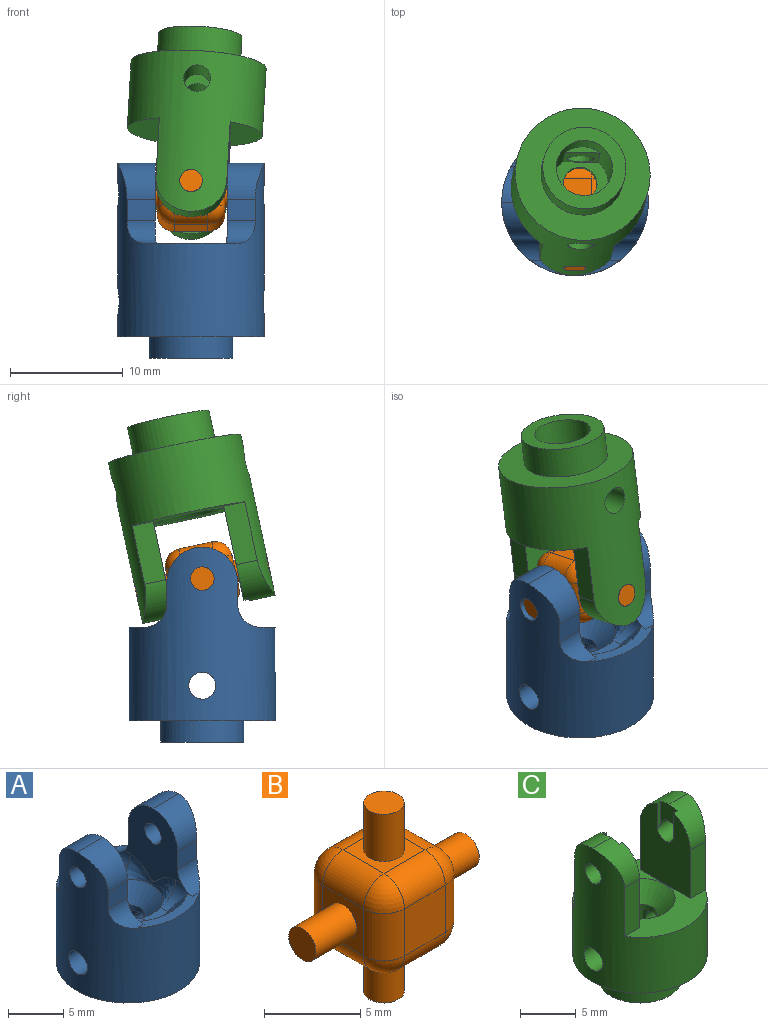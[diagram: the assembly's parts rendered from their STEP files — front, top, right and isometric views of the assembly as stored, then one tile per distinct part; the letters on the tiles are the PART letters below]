
ASSEMBLY  parts=3 mates=2
PART A: 42 faces, bbox 13x13x17.3 mm
  f0: plane 2.4x1.15mm, normal (0,0,1), area 2.2mm2, adj f23,f31,f36,f39
  f1: plane 2.4x1.15mm, normal (0,0,1), area 2.2mm2, adj f26,f31,f38,f41
  f2: plane 2.49x1.93mm, normal (0,1,0), area 4.8mm2, adj f4,f14,f29,f32
  f3: plane 2.49x1.93mm, normal (0,-1,0), area 4.8mm2, adj f4,f14,f30,f33
  f4: plane 8.06x7.39mm, normal (1,0,0), area 37mm2, adj f2,f3,f20,f29,f30,f32,f33,f39
  f5: plane 2.49x1.93mm, normal (0,1,0), area 4.8mm2, adj f6,f14,f27,f34
  f6: plane 8.06x7.39mm, normal (-1,0,0), area 37mm2, adj f5,f7,f19,f27,f28,f34,f35,f36
  f7: plane 2.49x1.93mm, normal (0,-1,0), area 4.8mm2, adj f6,f14,f28,f35
  f8: cylinder r=2.5mm len=6.6mm, axis (0,0,-1), area 71.9mm2, adj f10,f11,f13,f15,f16,f18
  f9: cylinder r=3.7mm len=7.4mm, axis (0,0,-1), area 44.2mm2, adj f10,f12
  f10: plane 7.4x7.4mm, normal (0,0,-1), area 23.4mm2, adj f8,f9
  f11: plane 3.13x0.55mm, normal (0,0,-1), area 1.2mm2, adj f8,f15
  f12: plane 13x13mm, normal (0,0,-1), area 89.7mm2, adj f9,f14
  f13: plane 4.7x3.13mm, normal (-1,0,0), area 10.2mm2, adj f8,f16,f18,f22
  f14: cylinder r=6.5mm len=15.4mm, axis (0,0,-1), area 416.5mm2, adj f2,f3,f5,f7,f12,f19,f20,f21
  f15: plane 4.7x3.13mm, normal (1,0,0), area 10.2mm2, adj f8,f11,f18,f21
  f16: plane 3.13x0.55mm, normal (0,0,-1), area 1.2mm2, adj f8,f13
  f17: cylinder r=1.5mm len=3mm, axis (0,0,-1), area 5.2mm2, adj f18,f31
  f18: plane 5x3.9mm, normal (0,0,-1), area 10.2mm2, adj f8,f13,f15,f17
  f19: cylinder r=1.05mm len=3.3mm, axis (1,0,0), area 21.8mm2, adj f6,f14
  f20: cylinder r=1.05mm len=3.3mm, axis (1,0,0), area 21.8mm2, adj f4,f14
  f21: cylinder r=1.2mm len=4.55mm, axis (1,0,0), area 34.3mm2, adj f14,f15
  f22: cylinder r=1.2mm len=4.55mm, axis (1,0,0), area 34.3mm2, adj f13,f14
  f23: sphere r=7mm, area 10.7mm2, adj f0,f24,f36,f39
  f24: plane 7.93x1.96mm, normal (0,0,1), area 7mm2, adj f14,f23,f33,f35,f36,f39
  f25: plane 7.93x1.96mm, normal (0,0,1), area 7mm2, adj f14,f26,f32,f34,f38,f41
  f26: sphere r=7mm, area 10.7mm2, adj f1,f25,f38,f41
  f27: cylinder r=3.2mm len=3.3mm, axis (1,0,0), area 14.4mm2, adj f5,f6,f14,f28
  f28: cylinder r=3.2mm len=3.3mm, axis (-1,0,0), area 14.4mm2, adj f6,f7,f14,f27
  f29: cylinder r=3.2mm len=3.3mm, axis (1,0,0), area 14.4mm2, adj f2,f4,f14,f30
  f30: cylinder r=3.2mm len=3.3mm, axis (-1,0,0), area 14.4mm2, adj f3,f4,f14,f29
  f31: cone r=1.5mm half-angle=45deg, axis (0,0,1), area 34.1mm2, adj f0,f1,f17,f37,f40
  f32: cylinder r=2mm len=2.59mm, axis (-1,0,0), area 6.2mm2, adj f2,f4,f14,f25,f41
  f33: cylinder r=2mm len=2.59mm, axis (1,0,0), area 6.2mm2, adj f3,f4,f14,f24,f39
  f34: cylinder r=2mm len=2.59mm, axis (-1,0,0), area 6.2mm2, adj f5,f6,f14,f25,f38
  f35: cylinder r=2mm len=2.59mm, axis (1,0,0), area 6.2mm2, adj f6,f7,f14,f24,f36
  f36: cylinder r=2mm len=2.24mm, axis (0,-1,0), area 3.7mm2, adj f0,f6,f23,f24,f35,f37
  f37: bspline ~5.83x2mm, area 9.6mm2, adj f6,f31,f36,f38
  f38: cylinder r=2mm len=2.24mm, axis (0,-1,0), area 3.7mm2, adj f1,f6,f25,f26,f34,f37
  f39: cylinder r=2mm len=2.24mm, axis (0,1,0), area 3.7mm2, adj f0,f4,f23,f24,f33,f40
  f40: bspline ~5.83x2mm, area 9.6mm2, adj f4,f31,f39,f41
  f41: cylinder r=2mm len=2.24mm, axis (0,1,0), area 3.7mm2, adj f1,f4,f25,f26,f32,f40
PART B: 34 faces, bbox 12x6x12 mm
  f0: plane 3x3mm, normal (-1,0,0), area 5.9mm2, adj f12,f22,f27,f30,f33
  f1: plane 3x3mm, normal (0,-1,0), area 9mm2, adj f19,f28,f29,f33
  f2: plane 3x3mm, normal (1,0,0), area 5.9mm2, adj f11,f14,f18,f19,f20
  f3: plane 3x3mm, normal (0,1,0), area 9mm2, adj f14,f17,f21,f22
  f4: plane 3x3mm, normal (0,0,1), area 5.5mm2, adj f8,f17,f18,f27,f28
  f5: plane 3x3mm, normal (0,0,-1), area 5.5mm2, adj f7,f20,f21,f29,f30
  f6: plane 2.1x2.1mm, normal (0,0,-1), area 3.5mm2, adj f7
  f7: cylinder r=1.05mm len=3mm, axis (0,0,-1), area 19.8mm2, adj f5,f6
  f8: cylinder r=1.05mm len=3mm, axis (0,0,-1), area 19.8mm2, adj f4,f9
  f9: plane 2.1x2.1mm, normal (0,0,1), area 3.5mm2, adj f8
  f10: plane 2x2mm, normal (1,0,0), area 3.1mm2, adj f11
  f11: cylinder r=1mm len=3mm, axis (-1,0,0), area 18.8mm2, adj f2,f10
  f12: cylinder r=1mm len=3mm, axis (-1,0,0), area 18.8mm2, adj f0,f13
  f13: plane 2x2mm, normal (-1,0,0), area 3.1mm2, adj f12
  f14: cylinder r=1.5mm len=3mm, axis (0,0,1), area 7.1mm2, adj f2,f3,f15,f16
  f15: sphere r=1.5mm, area 3.5mm2, adj f14,f17,f18
  f16: sphere r=1.5mm, area 3.5mm2, adj f14,f20,f21
  f17: cylinder r=1.5mm len=3mm, axis (1,0,0), area 7.1mm2, adj f3,f4,f15,f23
  f18: cylinder r=1.5mm len=3mm, axis (0,-1,0), area 7.1mm2, adj f2,f4,f15,f24
  f19: cylinder r=1.5mm len=3mm, axis (0,0,-1), area 7.1mm2, adj f1,f2,f24,f25
  f20: cylinder r=1.5mm len=3mm, axis (0,1,0), area 7.1mm2, adj f2,f5,f16,f25
  f21: cylinder r=1.5mm len=3mm, axis (-1,0,0), area 7.1mm2, adj f3,f5,f16,f26
  f22: cylinder r=1.5mm len=3mm, axis (0,0,-1), area 7.1mm2, adj f0,f3,f23,f26
  f23: sphere r=1.5mm, area 3.5mm2, adj f17,f22,f27
  f24: sphere r=1.5mm, area 3.5mm2, adj f18,f19,f28
  f25: sphere r=1.5mm, area 3.5mm2, adj f19,f20,f29
  f26: sphere r=1.5mm, area 3.5mm2, adj f21,f22,f30
  f27: cylinder r=1.5mm len=3mm, axis (0,1,0), area 7.1mm2, adj f0,f4,f23,f31
  f28: cylinder r=1.5mm len=3mm, axis (-1,0,0), area 7.1mm2, adj f1,f4,f24,f31
  f29: cylinder r=1.5mm len=3mm, axis (1,0,0), area 7.1mm2, adj f1,f5,f25,f32
  f30: cylinder r=1.5mm len=3mm, axis (0,-1,0), area 7.1mm2, adj f0,f5,f26,f32
  f31: sphere r=1.5mm, area 3.5mm2, adj f27,f28,f33
  f32: sphere r=1.5mm, area 3.5mm2, adj f29,f30,f33
  f33: cylinder r=1.5mm len=3mm, axis (0,0,1), area 7.1mm2, adj f0,f1,f31,f32
PART C: 37 faces, bbox 12x12x17.3 mm
  f0: plane 8.31x6.3mm, normal (1,0,0), area 41.8mm2, adj f3,f4,f16,f17,f22,f23,f25,f26
  f1: plane 8.31x6.3mm, normal (-1,0,0), area 41.8mm2, adj f2,f4,f18,f19,f27,f28,f30,f31
  f2: cylinder r=1mm len=2.8mm, axis (1,0,0), area 15.9mm2, adj f1,f11,f29,f30,f31
  f3: cylinder r=1mm len=2.8mm, axis (1,0,0), area 15.9mm2, adj f0,f11,f22,f23,f24
  f4: plane 12x10.21mm, normal (0,0,1), area 50.3mm2, adj f0,f1,f11,f16,f17,f18,f19,f36
  f5: cylinder r=2.5mm len=6.6mm, axis (0,0,-1), area 77.3mm2, adj f7,f8,f10,f12,f13,f15
  f6: cylinder r=3.7mm len=7.4mm, axis (0,0,-1), area 62.8mm2, adj f7,f9
  f7: plane 7.4x7.4mm, normal (0,0,-1), area 23.4mm2, adj f5,f6
  f8: plane 3.13x0.55mm, normal (0,0,-1), area 1.2mm2, adj f5,f12
  f9: plane 12x12mm, normal (0,0,-1), area 70.1mm2, adj f6,f11
  f10: plane 3.9x3.13mm, normal (-1,0,0), area 7.7mm2, adj f5,f13,f15,f21
  f11: cylinder r=6mm len=14.6mm, axis (0,0,-1), area 317.6mm2, adj f2,f3,f4,f9,f16,f17,f18,f19
  f12: plane 3.9x3.13mm, normal (1,0,0), area 7.7mm2, adj f5,f8,f15,f20
  f13: plane 3.13x0.55mm, normal (0,0,-1), area 1.2mm2, adj f5,f10
  f14: cylinder r=1.5mm len=3mm, axis (0,0,-1), area 5.2mm2, adj f15,f36
  f15: plane 5x3.9mm, normal (0,0,-1), area 10.2mm2, adj f5,f10,f12,f14
  f16: plane 5.3x1.91mm, normal (0,1,0), area 10.1mm2, adj f0,f4,f11,f34
  f17: plane 5.3x1.91mm, normal (0,-1,0), area 10.1mm2, adj f0,f4,f11,f35
  f18: plane 5.3x1.91mm, normal (0,1,0), area 10.1mm2, adj f1,f4,f11,f32
  f19: plane 5.3x1.91mm, normal (0,-1,0), area 10.1mm2, adj f1,f4,f11,f33
  f20: cylinder r=1.2mm len=4.05mm, axis (1,0,0), area 30.1mm2, adj f11,f12
  f21: cylinder r=1.2mm len=4.05mm, axis (1,0,0), area 30.1mm2, adj f10,f11
  f22: plane 0.45x0.05mm, normal (0,0,1), area 0mm2, adj f0,f3,f24,f25
  f23: plane 0.45x0.05mm, normal (0,0,1), area 0mm2, adj f0,f3,f24,f26
  f24: plane 2.8x2.1mm, normal (1,0,0), area 4.2mm2, adj f3,f22,f23,f25,f26,f34,f35
  f25: plane 2.61x0.45mm, normal (0,1,0), area 1.2mm2, adj f0,f22,f24,f35
  f26: plane 2.61x0.45mm, normal (0,-1,0), area 1.2mm2, adj f0,f23,f24,f34
  f27: plane 2.61x0.45mm, normal (0,-1,0), area 1.2mm2, adj f1,f29,f31,f32
  f28: plane 2.61x0.45mm, normal (0,1,0), area 1.2mm2, adj f1,f29,f30,f33
  f29: plane 2.8x2.1mm, normal (-1,0,0), area 4.2mm2, adj f2,f27,f28,f30,f31,f32,f33
  f30: plane 0.45x0.05mm, normal (0,0,1), area 0mm2, adj f1,f2,f28,f29
  f31: plane 0.45x0.05mm, normal (0,0,1), area 0mm2, adj f1,f2,f27,f29
  f32: cylinder r=3.2mm len=3.2mm, axis (1,0,0), area 11.3mm2, adj f1,f11,f18,f27,f29,f33
  f33: cylinder r=3.2mm len=3.2mm, axis (-1,0,0), area 11.3mm2, adj f1,f11,f19,f28,f29,f32
  f34: cylinder r=3.2mm len=3.2mm, axis (1,0,0), area 11.3mm2, adj f0,f11,f16,f24,f26,f35
  f35: cylinder r=3.2mm len=3.2mm, axis (-1,0,0), area 11.3mm2, adj f0,f11,f17,f24,f25,f34
  f36: cone r=1.5mm half-angle=45deg, axis (0,0,1), area 34.1mm2, adj f4,f14
PLACE A at identity fixed
PLACE B rot(axis=(-0.61,0.5,-0.61),127.2deg) t=(-3,3.56,16.81)mm
PLACE C rot(axis=(0.71,0.7,-0.09),173.8deg) t=(0.82,3.02,28.66)mm
MATE revolute B.f11 <-> C.f2  axis (0,0.98,-0.21) through (0,-2.93,15.13)mm
MATE revolute B.f7 <-> A.f19  axis (-1,0,0) through (3,0,14.5)mm
